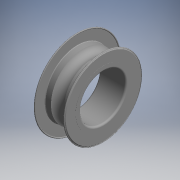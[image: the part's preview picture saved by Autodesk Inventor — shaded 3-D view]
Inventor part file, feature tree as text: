
AUTODESK INVENTOR PART (.ipt)
format: ipt  version: 2017.3 (Build 213256000, 256)  size: 206,336 bytes
history: native  units: mm (DEFAULTED — no unit token found)
features: revolve x3, sketch x3
ambient origin geometry x8: Origin, YZ Plane, XZ Plane, XY Plane, X Axis, Y Axis, Z Axis, Center Point
bodies: Solid1 (feature_tree)
feature tree (6):
  revolve  "Revolution1"  Angle=360.0deg
  revolve  "Revolution2"  [1 undecoded]
  revolve  "Revolution3"  [1 undecoded]
  sketch  "Sketch_4"  dims[d0=360.0deg d1=360.0deg]
  sketch  "Sketch_5"  dims[d2=360.0deg]
  sketch  "Sketch_6"
note: 2 required parameter values undecoded (feature->parameter linkage not recoverable at this tier; creation-order binding heuristic only, values carry confidence <= 0.55)
